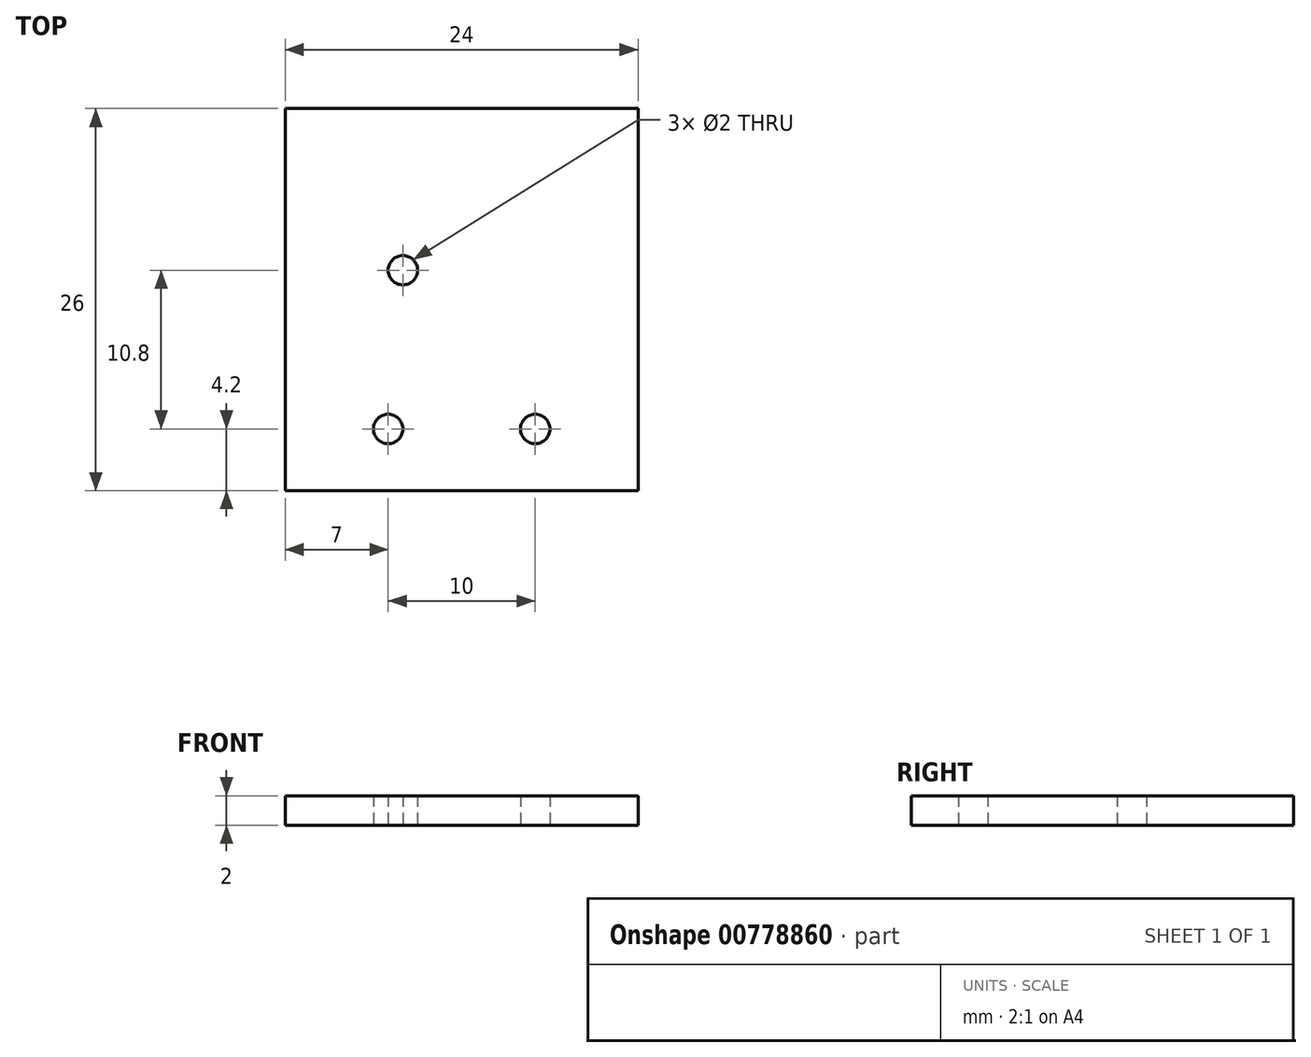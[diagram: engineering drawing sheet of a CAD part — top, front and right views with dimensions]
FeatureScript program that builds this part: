
annotation { "Feature Type Name" : "Feature", "Feature Type Description" : "" }
export const myFeature = defineFeature(function(context is Context, id is Id, definition is map)
    precondition{}
    {
        {
            var Q0;
            Q0=qCreatedBy(makeId("Top.planeOp"),FACE);
            var sketch = newSketch(context, id + "F0", { "sketchPlane" : qUnion([Q0])});
            skLineSegment(sketch, "E0.bottom", {"start": v(-24, 26) * mm, "end": v(0, 26) * mm});
            skLineSegment(sketch, "E0.top", {"start": v(-24, 0) * mm, "end": v(0, 0) * mm});
            skLineSegment(sketch, "E0.left", {"start": v(-24, 26) * mm, "end": v(-24, 0) * mm});
            skLineSegment(sketch, "E0.right", {"start": v(0, 26) * mm, "end": v(0, 0) * mm});
            skCircle(sketch, "E1", {"center": v(-16, 15) * mm, "radius": 1 * mm});
            skCircle(sketch, "E2", {"center": v(-17, 4.2) * mm, "radius": 1 * mm});
            skCircle(sketch, "E3", {"center": v(-7, 4.2) * mm, "radius": 1 * mm});
            skSolve(sketch);
        }
        {
            var Q0;
            Q0=makeQuery(id+"F0.imprint","IMPRINT",FACE,{"disambiguationData":[TD([[makeQuery(id+"F0.imprint","IMPRINT",EDGE,{"derivedFrom":sQuery(id+"F0.wireOp",EDGE,"E0.bottom")}),-1.0]])]});
            extrude(context, id + "F1", {"entities" : qUnion([Q0]), "depth" : 2 * mm, "offsetDistance" : 25 * mm});
        }
    });
